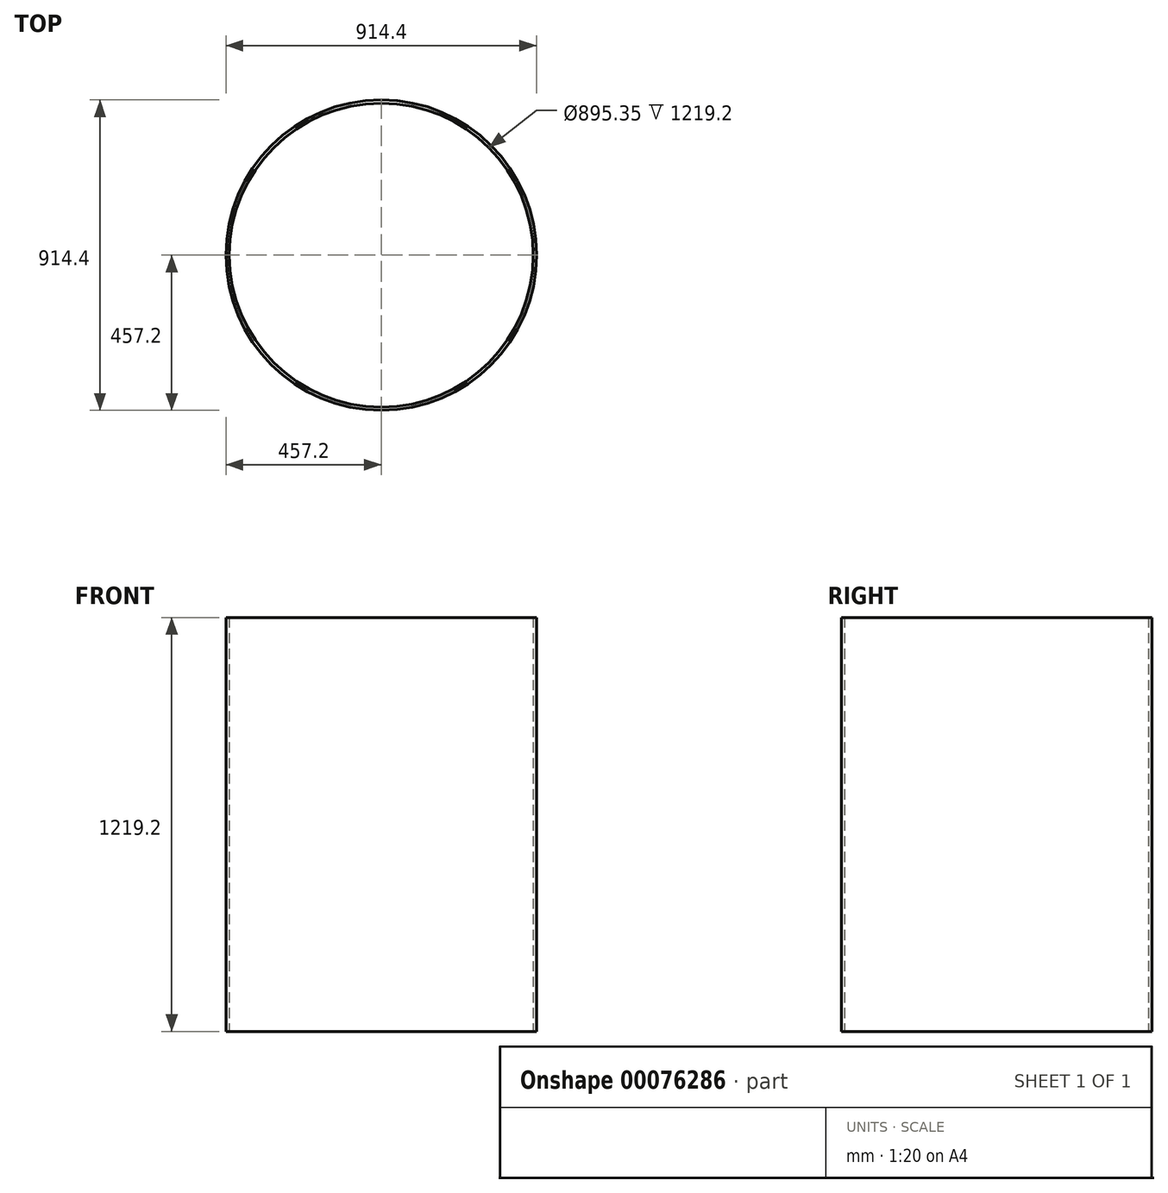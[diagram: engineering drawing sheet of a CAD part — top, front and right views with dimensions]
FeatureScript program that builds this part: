
annotation { "Feature Type Name" : "Feature", "Feature Type Description" : "" }
export const myFeature = defineFeature(function(context is Context, id is Id, definition is map)
    precondition{}
    {
        {
            var Q0;
            Q0=qCreatedBy(makeId("Top.planeOp"),FACE);
            var sketch = newSketch(context, id + "F0", { "sketchPlane" : qUnion([Q0])});
            skCircle(sketch, "E0", {"center": v(0, 0) * mm, "radius": 457.2 * mm});
            skCircle(sketch, "E1", {"center": v(0, 0) * mm, "radius": 447.68 * mm});
            skSolve(sketch);
        }
        {
            var Q0;
            Q0 = qSketchRegion(id + "F0", true);
            extrude(context, id + "F1", {"entities" : qUnion([Q0]), "depth" : 1219.2 * mm});
        }
    });
